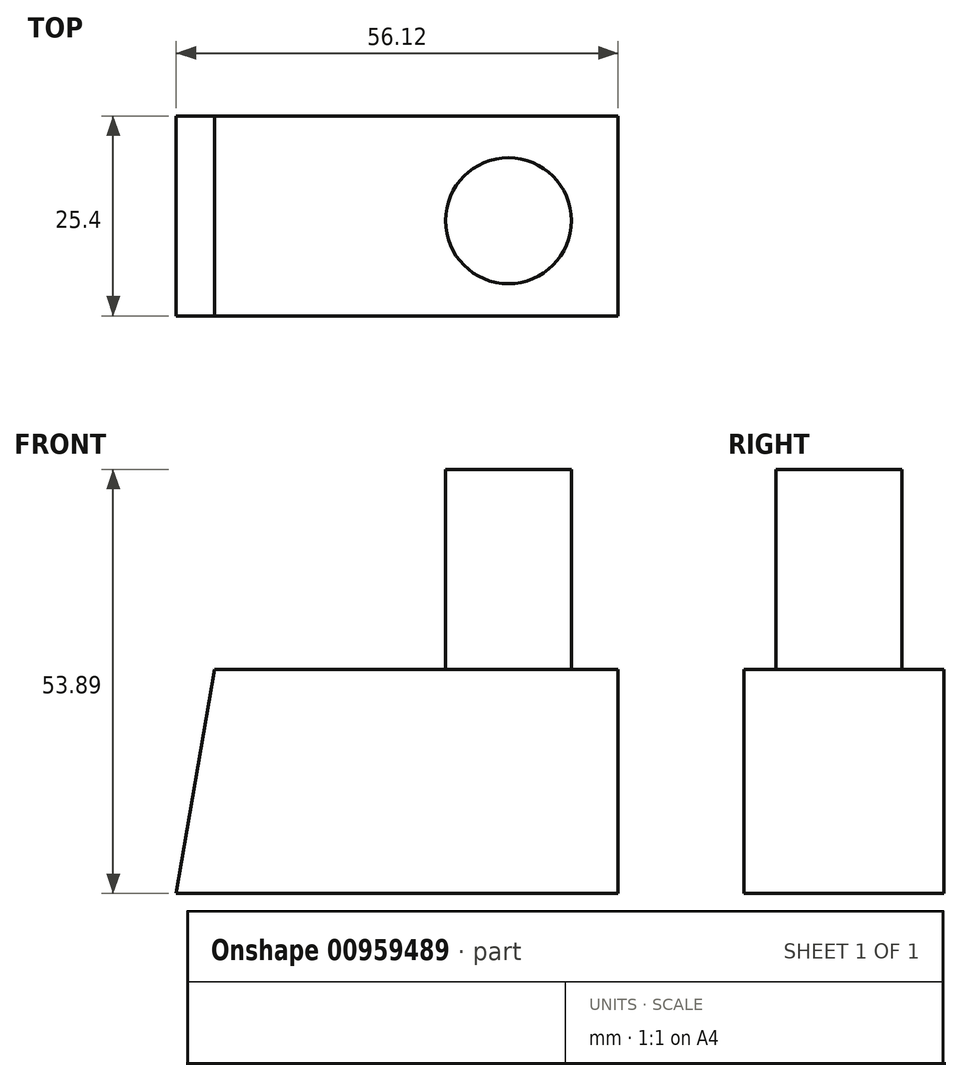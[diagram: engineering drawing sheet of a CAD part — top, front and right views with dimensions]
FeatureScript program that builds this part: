
annotation { "Feature Type Name" : "Feature", "Feature Type Description" : "" }
export const myFeature = defineFeature(function(context is Context, id is Id, definition is map)
    precondition{}
    {
        {
            var Q0;
            Q0=qCreatedBy(makeId("Front.planeOp"),FACE);
            var sketch = newSketch(context, id + "F0", { "sketchPlane" : qUnion([Q0])});
            skLineSegment(sketch, "E0", {"start": v(-25.62, 14.57) * mm, "end": v(25.62, 14.57) * mm});
            skLineSegment(sketch, "E1", {"start": v(25.62, 14.57) * mm, "end": v(25.62, -13.92) * mm});
            skLineSegment(sketch, "E2", {"start": v(25.62, -13.92) * mm, "end": v(-30.5, -13.92) * mm});
            skLineSegment(sketch, "E3", {"start": v(-30.5, -13.92) * mm, "end": v(-25.62, 14.57) * mm});
            skLineSegment(sketch, "E4", {"start": v(-30.5, -13.92) * mm, "end": v(-25.62, -13.92) * mm});
            skSolve(sketch);
        }
        {
            var Q0;
            Q0=makeQuery(id+"F0.imprint","IMPRINT",FACE,{"disambiguationData":[TD([[makeQuery(id+"F0.imprint","IMPRINT",EDGE,{"derivedFrom":sQuery(id+"F0.wireOp",EDGE,"E0")}),-1.0]])]});
            extrude(context, id + "F1", {"entities" : qUnion([Q0]), "depth" : 25.4 * mm, "offsetDistance" : 25.4 * mm});
        }
        {
            var Q0;
            Q0=makeQuery(id+"F1.opExtrude","SWEPT_FACE",FACE,{"disambiguationData":[OSD([sQuery(id+"F0.wireOp",EDGE,"E0")])]});
            var sketch = newSketch(context, id + "F2", { "sketchPlane" : qUnion([Q0])});
            skCircle(sketch, "E5", {"center": v(11.7, -13.32) * mm, "radius": 8 * mm});
            skSolve(sketch);
        }
        {
            var Q0;
            Q0 = qSketchRegion(id + "F2", true);
            extrude(context, id + "F3", {"entities" : qUnion([Q0]), "operationType" : NewBodyOperationType.ADD, "depth" : 25.4 * mm, "offsetDistance" : 25.4 * mm});
        }
    });
